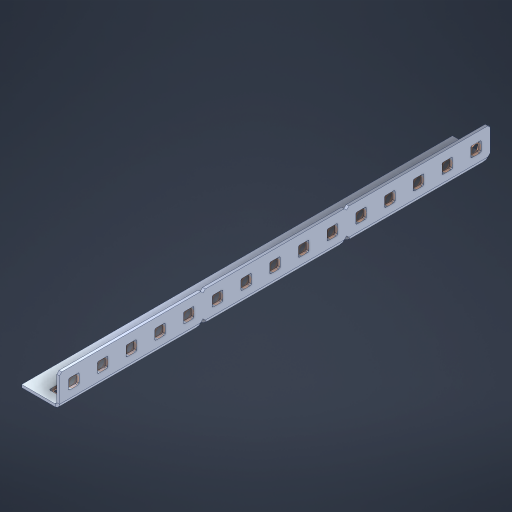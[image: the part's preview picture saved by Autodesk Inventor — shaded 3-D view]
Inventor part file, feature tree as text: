
AUTODESK INVENTOR PART (.ipt)
format: ipt  version: 2023 (Build 270158000, 158)  size: 661,504 bytes
history: native  units: in
note: dims shown in document units (in); Inventor stores cm internally (conversion verified against a paired STEP export)
features: other x35, extrude x29, sheet_metal_op x10, sketch x8, mirror x1, pattern_linear x1, chamfer x1
ambient origin geometry x8: Origin, YZ Plane, XZ Plane, XY Plane, X Axis, Y Axis, Z Axis, Center Point
bodies: Solid1 (feature_tree), Body (feature_tree)
feature tree (85):
  other  "Flange Pattern Plane"
  sheet_metal_op  "Flange Pattern"
  sheet_metal_op  "Body Pattern"
  other  "Arc Length"
  mirror  "Notch Mirror"
  pattern_linear  "Notch Pattern"  Spacing1=0.1875in  [1 undecoded]
  chamfer  "End Chamfer"
  extrude  "Half Cut"  Depth=0.0469in
  sketch  "Sketch1"  dims[d0=2.5in]
  other  "Plate1"
  sketch  "Sketch2"  dims[d1=7.5in]
  other  "Plate2"
  sheet_metal_op  "Bend1"
  sheet_metal_op  "Corner1"
  sketch  "Sketch3"  dims[d2=0.0469in]
  other  "Flange Pattern Sketch"
  sketch  "Sketch7"  dims[d3=0.0469in]
  other  "Srf1"
  other  "Srf2"
  sketch  "Sketch8"  dims[d4=0.0234in]
  sketch  "Sketch9"  dims[d5=0.0938in]
  other  "Srf91"
  sheet_metal_op  "Body Pattern Sketch"
  other  "Srf92"
  sketch  "Sketch13"  dims[d6=0.0469in]
  sketch  "Sketch14"  dims[d7=0.5in d8=90.0deg d9=0.0312in d10=0.1875in d11=0.0469in d12=0.0469in d16=0.182in d17=0.02in d18=0.0469in d19=0.0in d20=0.25in d21=0.25in d46=0.172in d47=1.0in d48=0.0in d49=0.182in d50=0.02in d51=0.25in d52=0.25in d53=0.0469in d54=0.0in d55=0.172in d56=1.0in d57=0.0in d60=5.9055in d62=0.5in d63=0.3937in d65=0.5in d85=0.1227in d86=0.1659in d88=0.04in d89=0.0469in d90=0.0in d91=0.04in d92=0.0491in d95=2.5in d96=0.04in d97=0.25in d98=45.0deg d101=0.0in d102=2.497in d131=0.5in d132=5.9055in d134=0.5in d139=0.5in]
  other  "Srf856"
  other  "Srf1310"
  other  "Srf1311"
  other  "Srf1312"
  other  "Srf1376"
  other  "Srf1377"
  other  "Srf1728"
  other  "Srf1755"
  other  "Srf1878"
  other  "Srf1879"
  other  "Srf1880"
  other  "Srf1881"
  other  "Srf1882"
  other  "Srf1883"
  other  "Srf1884"
  other  "Srf1885"
  other  "Srf1886"
  other  "Srf1942"
  other  "Srf1943"
  other  "Srf1944"
  other  "Srf1945"
  other  "Srf1946"
  other  "Srf1947"
  other  "Srf1948"
  other  "Srf1949"
  other  "Srf1950"
  sheet_metal_op  "Flange Stamp"
  sheet_metal_op  "Flange Circle"
  sheet_metal_op  "Body Stamp"
  sheet_metal_op  "Body Circle"
  sheet_metal_op  "Notch"
  extrude  "ExtrusionSrf2"  Depth=0.0469in
  extrude  "ExtrusionSrf92"  Depth=0.0469in
  extrude  "ExtrusionSrf856"  Depth=0.02in
  extrude  "ExtrusionSrf1310"  Depth=0.0469in
  extrude  "ExtrusionSrf1311"  TaperAngle=0.0deg  [1 undecoded]
  extrude  "ExtrusionSrf1312"  Depth=0.0469in
  extrude  "ExtrusionSrf1376"  Depth=0.0469in
  extrude  "ExtrusionSrf1377"  Depth=0.0469in
  extrude  "ExtrusionSrf1728"  Depth=0.0469in TaperAngle=0.0deg
  extrude  "ExtrusionSrf1755"  Depth=0.0469in
  extrude  "ExtrusionSrf1878"  Depth=0.02in
  extrude  "ExtrusionSrf1879"  Depth=0.0469in
  extrude  "ExtrusionSrf1880"  Depth=0.0469in
  extrude  "ExtrusionSrf1881"  Depth=0.0469in
  extrude  "ExtrusionSrf1882"  TaperAngle=0.0deg  [1 undecoded]
  extrude  "ExtrusionSrf1883"  Depth=0.0469in
  extrude  "ExtrusionSrf1884"  Depth=0.0469in TaperAngle=0.0deg
  extrude  "ExtrusionSrf1885"  Depth=0.0469in
  extrude  "ExtrusionSrf1886"  Depth=0.3937in
  extrude  "ExtrusionSrf1942"  Depth=0.0469in
  extrude  "ExtrusionSrf1943"  Depth=0.0469in
  extrude  "ExtrusionSrf1944"  Depth=0.0469in
  extrude  "ExtrusionSrf1945"  Depth=0.0469in
  extrude  "ExtrusionSrf1946"  TaperAngle=0.0deg  [1 undecoded]
  extrude  "ExtrusionSrf1947"  Depth=0.0469in
  extrude  "ExtrusionSrf1948"  Depth=0.0469in
  extrude  "ExtrusionSrf1949"  Depth=0.0469in
  extrude  "ExtrusionSrf1950"  Depth=0.0469in TaperAngle=45.0deg
note: 4 required parameter values undecoded (feature->parameter linkage not recoverable at this tier; creation-order binding heuristic only, values carry confidence <= 0.55)
